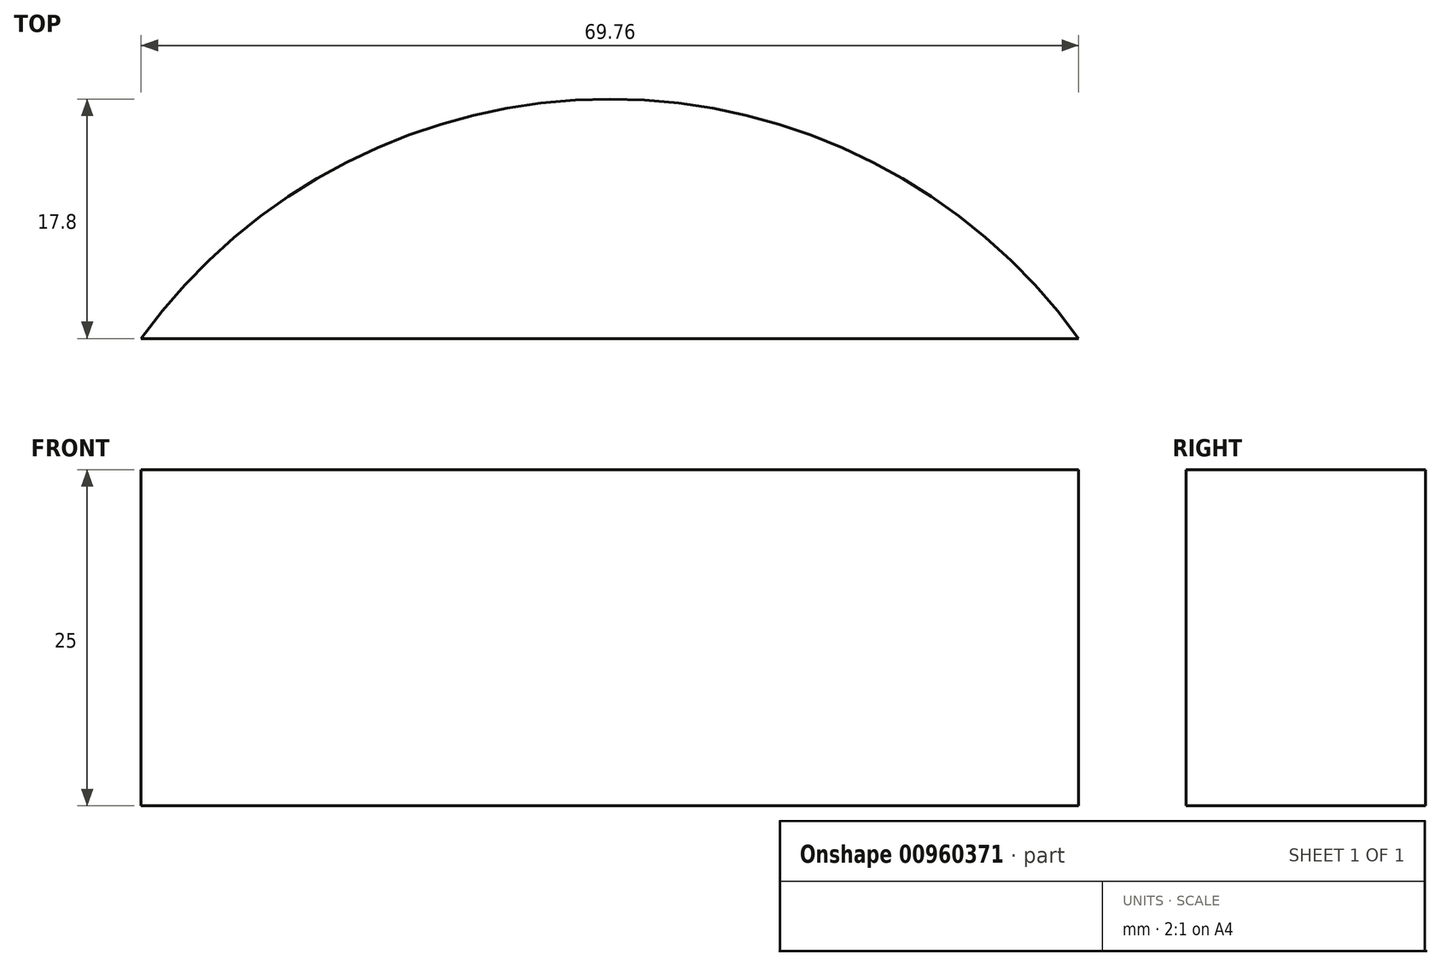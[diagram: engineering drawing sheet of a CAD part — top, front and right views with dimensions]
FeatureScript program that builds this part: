
annotation { "Feature Type Name" : "Feature", "Feature Type Description" : "" }
export const myFeature = defineFeature(function(context is Context, id is Id, definition is map)
    precondition{}
    {
        {
            var Q0;
            Q0=qCreatedBy(makeId("Top.planeOp"),FACE);
            var sketch = newSketch(context, id + "F0", { "sketchPlane" : qUnion([Q0])});
            skLineSegment(sketch, "E0.bottom", {"start": v(-34.88, 34.7) * mm, "end": v(34.88, 34.7) * mm});
            skLineSegment(sketch, "E0.top", {"start": v(-34.88, -34.7) * mm, "end": v(34.88, -34.7) * mm});
            skLineSegment(sketch, "E0.left", {"start": v(-34.88, 34.7) * mm, "end": v(-34.88, -34.7) * mm});
            skLineSegment(sketch, "E0.right", {"start": v(34.88, 34.7) * mm, "end": v(34.88, -34.7) * mm});
            skPoint(sketch, "E0.middle", {"position": v(0, 0) * mm});
            skPoint(sketch, "E1.0.midPoint", {"position": v(0, 52.5) * mm});
            skArc(sketch, "E2", {"start": v(34.88, 34.7) * mm, "mid": v(0, 52.5) * mm, "end": v(-34.88, 34.7) * mm});
            skArc(sketch, "E3", {"start": v(-34.88, 34.7) * mm, "mid": v(-15.3, 39.4) * mm, "end": v(0, 52.5) * mm, "construction": true});
            skArc(sketch, "E4", {"start": v(0, 52.5) * mm, "mid": v(15.3, 39.4) * mm, "end": v(34.88, 34.7) * mm, "construction": true});
            skSolve(sketch);
        }
        {
            var Q0;
            Q0=makeQuery(id+"F0.imprint","IMPRINT",FACE,{"disambiguationData":[TD([[makeQuery(id+"F0.imprint","IMPRINT",EDGE,{"derivedFrom":sQuery(id+"F0.wireOp",EDGE,"E0.bottom")}),1.0]])]});
            extrude(context, id + "F1", {"entities" : qUnion([Q0]), "depth" : 25 * mm, "offsetDistance" : 25 * mm});
        }
    });
